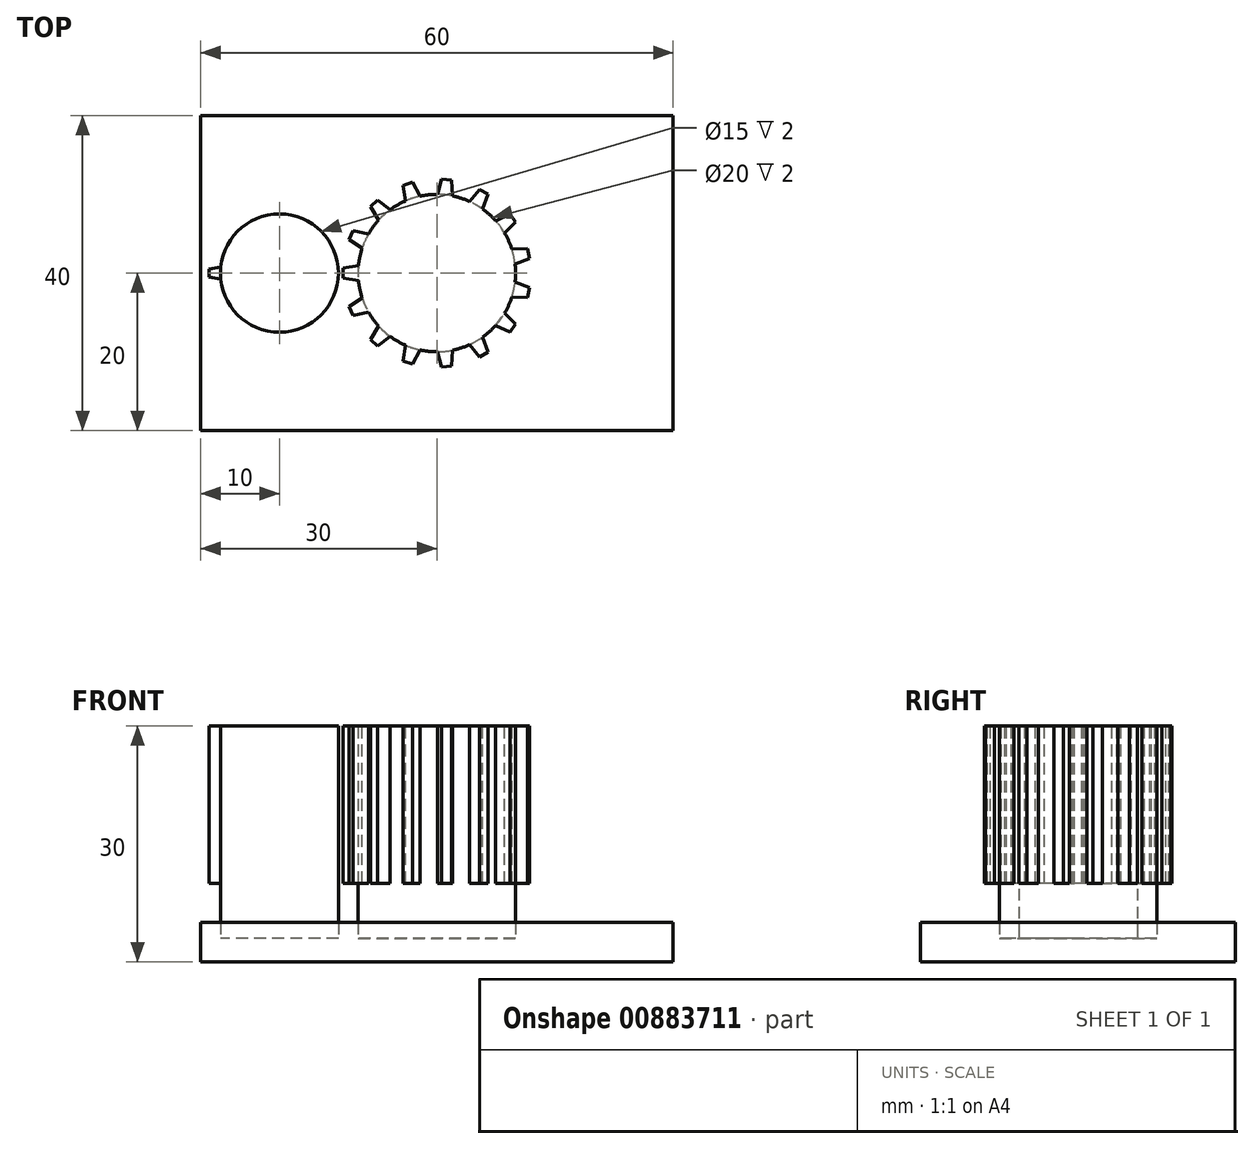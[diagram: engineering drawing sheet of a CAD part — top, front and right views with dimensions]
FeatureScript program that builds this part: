
annotation { "Feature Type Name" : "Feature", "Feature Type Description" : "" }
export const myFeature = defineFeature(function(context is Context, id is Id, definition is map)
    precondition{}
    {
        {
            var Q0;
            Q0=qCreatedBy(makeId("Top.planeOp"),FACE);
            var sketch = newSketch(context, id + "F0", { "sketchPlane" : qUnion([Q0])});
            skLineSegment(sketch, "E0.bottom", {"start": v(-30, 20) * mm, "end": v(30, 20) * mm});
            skLineSegment(sketch, "E0.top", {"start": v(-30, -20) * mm, "end": v(30, -20) * mm});
            skLineSegment(sketch, "E0.left", {"start": v(-30, 20) * mm, "end": v(-30, -20) * mm});
            skLineSegment(sketch, "E0.right", {"start": v(30, 20) * mm, "end": v(30, -20) * mm});
            skPoint(sketch, "E0.middle", {"position": v(0, 0) * mm});
            skSolve(sketch);
        }
        {
            var Q0;
            Q0 = qSketchRegion(id + "F0", true);
            extrude(context, id + "F1", {"entities" : qUnion([Q0]), "depth" : 5 * mm, "offsetDistance" : 25 * mm});
        }
        {
            var Q0;
            Q0=makeQuery(id+"F1.opExtrude","CAP_FACE",FACE,{"disambiguationData":[OSD([sQuery(id+"F0.wireOp",EDGE,"E0.bottom"),sQuery(id+"F0.wireOp",EDGE,"E0.top"),sQuery(id+"F0.wireOp",EDGE,"E0.left"),sQuery(id+"F0.wireOp",EDGE,"E0.right")])],"isStart":false});
            var sketch = newSketch(context, id + "F2", { "sketchPlane" : qUnion([Q0])});
            skCircle(sketch, "E1", {"center": v(-20, 0) * mm, "radius": 7.5 * mm});
            skSolve(sketch);
        }
        {
            var Q0;
            Q0 = qSketchRegion(id + "F2", true);
            extrude(context, id + "F3", {"entities" : qUnion([Q0]), "depth" : 25 * mm, "offsetDistance" : 25 * mm, "hasSecondDirection" : true, "secondDirectionOppositeDirection" : true, "secondDirectionDepth" : 2 * mm});
        }
        {
            var Q0;
            Q0=makeQuery(id+"F3.opExtrude","SWEPT_BODY",BODY,{"disambiguationData":[OSD([sQuery(id+"F2.wireOp",EDGE,"E1")])]});
            var Q1;
            Q1=makeQuery(id+"F1.opExtrude","SWEPT_BODY",BODY,{"disambiguationData":[OSD([sQuery(id+"F0.wireOp",EDGE,"E0.bottom"),sQuery(id+"F0.wireOp",EDGE,"E0.top"),sQuery(id+"F0.wireOp",EDGE,"E0.left"),sQuery(id+"F0.wireOp",EDGE,"E0.right")])]});
            booleanBodies(context, id + "F4", {"operationType" : BooleanOperationType.SUBTRACTION, "tools" : qUnion([Q0]), "targets" : qUnion([Q1]), "keepTools" : true});
        }
        {
            var Q0;
            Q0=makeQuery(id+"F1.opExtrude","CAP_FACE",FACE,{"disambiguationData":[OSD([sQuery(id+"F0.wireOp",EDGE,"E0.bottom"),sQuery(id+"F0.wireOp",EDGE,"E0.top"),sQuery(id+"F0.wireOp",EDGE,"E0.left"),sQuery(id+"F0.wireOp",EDGE,"E0.right")])],"isStart":false});
            var sketch = newSketch(context, id + "F5", { "sketchPlane" : qUnion([Q0])});
            skCircle(sketch, "E2", {"center": v(0, 0) * mm, "radius": 10 * mm});
            skSolve(sketch);
        }
        {
            var Q0;
            Q0 = qSketchRegion(id + "F5", true);
            extrude(context, id + "F6", {"entities" : qUnion([Q0]), "depth" : 25 * mm, "offsetDistance" : 25 * mm, "hasSecondDirection" : true, "secondDirectionOppositeDirection" : true, "secondDirectionDepth" : 2 * mm});
        }
        {
            var Q0;
            Q0=makeQuery(id+"F6.opExtrude","SWEPT_BODY",BODY,{"disambiguationData":[OSD([sQuery(id+"F5.wireOp",EDGE,"E2")])]});
            var Q1;
            Q1=makeQuery(id+"F1.opExtrude","SWEPT_BODY",BODY,{"disambiguationData":[OSD([sQuery(id+"F0.wireOp",EDGE,"E0.bottom"),sQuery(id+"F0.wireOp",EDGE,"E0.top"),sQuery(id+"F0.wireOp",EDGE,"E0.left"),sQuery(id+"F0.wireOp",EDGE,"E0.right")])]});
            booleanBodies(context, id + "F7", {"operationType" : BooleanOperationType.SUBTRACTION, "tools" : qUnion([Q0]), "targets" : qUnion([Q1]), "keepTools" : true});
        }
        {
            var Q0;
            Q0=makeQuery(id+"F3.opExtrude","CAP_FACE",FACE,{"disambiguationData":[OSD([sQuery(id+"F2.wireOp",EDGE,"E1")])],"isStart":false});
            var sketch = newSketch(context, id + "F8", { "sketchPlane" : qUnion([Q0])});
            skLineSegment(sketch, "E3", {"start": v(-27.46, 0.76) * mm, "end": v(-28.94, 0.5) * mm});
            skLineSegment(sketch, "E4", {"start": v(-28.94, 0.5) * mm, "end": v(-28.94, 0) * mm});
            skLineSegment(sketch, "E5.MirrorCS", {"start": v(-27.46, -0.76) * mm, "end": v(-28.94, -0.5) * mm});
            skLineSegment(sketch, "E6.MirrorCS", {"start": v(-28.94, -0.5) * mm, "end": v(-28.94, 0) * mm});
            skCircle(sketch, "E7.0", {"center": v(-20, 0) * mm, "radius": 7.5 * mm});
            skSolve(sketch);
        }
        {
            var Q0;
            Q0 = qSketchRegion(id + "F8", true);
            extrude(context, id + "F9", {"entities" : qUnion([Q0]), "oppositeDirection" : true, "depth" : 20 * mm, "offsetDistance" : 25 * mm});
        }
        {
            var Q0;
            Q0=makeQuery(id+"F3.opExtrude","SWEPT_BODY",BODY,{"disambiguationData":[OSD([sQuery(id+"F2.wireOp",EDGE,"E1")])]});
            var Q1;
            Q1=makeQuery(id+"F9.opExtrude","SWEPT_BODY",BODY,{"disambiguationData":[OSD([sQuery(id+"F8.wireOp",EDGE,"E3"),sQuery(id+"F8.wireOp",EDGE,"E4"),sQuery(id+"F8.wireOp",EDGE,"E5.MirrorCS"),sQuery(id+"F8.wireOp",EDGE,"E6.MirrorCS"),sQuery(id+"F8.wireOp",EDGE,"E7.0")])]});
            booleanBodies(context, id + "F10", {"operationType" : BooleanOperationType.SUBTRACTION, "tools" : qUnion([Q0]), "targets" : qUnion([Q1]), "keepTools" : true});
        }
        {
            var Q0;
            Q0=makeQuery(id+"F6.opExtrude","CAP_FACE",FACE,{"disambiguationData":[OSD([sQuery(id+"F5.wireOp",EDGE,"E2")])],"isStart":false});
            var sketch = newSketch(context, id + "F11", { "sketchPlane" : qUnion([Q0])});
            skCircle(sketch, "E8.0", {"center": v(0, 0) * mm, "radius": 10 * mm});
            skLineSegment(sketch, "E9", {"start": v(-9.95, 0.97) * mm, "end": v(-11.92, 0.63) * mm});
            skLineSegment(sketch, "E10", {"start": v(-11.92, 0.62) * mm, "end": v(-11.92, 0) * mm});
            skLineSegment(sketch, "E11.MirrorCS", {"start": v(-9.95, -0.97) * mm, "end": v(-11.92, -0.63) * mm});
            skLineSegment(sketch, "E12.MirrorCS", {"start": v(-11.92, -0.62) * mm, "end": v(-11.92, 0) * mm});
            skLineSegment(sketch, "E13.1.0", {"start": v(-9.49, -3.16) * mm, "end": v(-11.15, -4.28) * mm});
            skLineSegment(sketch, "E13.1.1", {"start": v(-11.15, -4.28) * mm, "end": v(-10.9, -4.85) * mm});
            skLineSegment(sketch, "E13.1.2", {"start": v(-10.64, -5.42) * mm, "end": v(-10.9, -4.85) * mm});
            skLineSegment(sketch, "E13.1.3", {"start": v(-8.7, -4.94) * mm, "end": v(-10.64, -5.42) * mm});
            skLineSegment(sketch, "E13.2.0", {"start": v(-7.38, -6.75) * mm, "end": v(-8.44, -8.44) * mm});
            skLineSegment(sketch, "E13.2.1", {"start": v(-8.44, -8.44) * mm, "end": v(-7.98, -8.86) * mm});
            skLineSegment(sketch, "E13.2.2", {"start": v(-7.51, -9.28) * mm, "end": v(-7.98, -8.86) * mm});
            skLineSegment(sketch, "E13.2.3", {"start": v(-5.94, -8.05) * mm, "end": v(-7.51, -9.28) * mm});
            skLineSegment(sketch, "E14.2.3.0", {"start": v(-4, -9.17) * mm, "end": v(-4.28, -11.15) * mm});
            skLineSegment(sketch, "E14.3.3.0", {"start": v(-4.28, -11.15) * mm, "end": v(-3.68, -11.34) * mm});
            skLineSegment(sketch, "E14.6.3.0", {"start": v(-3.09, -11.53) * mm, "end": v(-3.68, -11.34) * mm});
            skLineSegment(sketch, "E14.9.3.0", {"start": v(-2.15, -9.77) * mm, "end": v(-3.09, -11.53) * mm});
            skLineSegment(sketch, "E14.2.4.0", {"start": v(0.07, -10) * mm, "end": v(0.62, -11.92) * mm});
            skLineSegment(sketch, "E14.3.4.0", {"start": v(0.62, -11.92) * mm, "end": v(1.25, -11.86) * mm});
            skLineSegment(sketch, "E14.6.4.0", {"start": v(1.87, -11.8) * mm, "end": v(1.25, -11.86) * mm});
            skLineSegment(sketch, "E14.9.4.0", {"start": v(2, -9.8) * mm, "end": v(1.87, -11.8) * mm});
            skLineSegment(sketch, "E14.2.5.0", {"start": v(4.13, -9.1) * mm, "end": v(5.42, -10.64) * mm});
            skLineSegment(sketch, "E14.3.5.0", {"start": v(5.42, -10.64) * mm, "end": v(5.96, -10.32) * mm});
            skLineSegment(sketch, "E14.6.5.0", {"start": v(6.5, -10.01) * mm, "end": v(5.96, -10.32) * mm});
            skLineSegment(sketch, "E14.9.5.0", {"start": v(5.82, -8.13) * mm, "end": v(6.5, -10.01) * mm});
            skLineSegment(sketch, "E14.2.6.0", {"start": v(7.48, -6.64) * mm, "end": v(9.28, -7.51) * mm});
            skLineSegment(sketch, "E14.3.6.0", {"start": v(9.28, -7.51) * mm, "end": v(9.65, -7) * mm});
            skLineSegment(sketch, "E14.6.6.0", {"start": v(10.01, -6.5) * mm, "end": v(9.65, -7) * mm});
            skLineSegment(sketch, "E14.9.6.0", {"start": v(8.62, -5.06) * mm, "end": v(10.01, -6.5) * mm});
            skLineSegment(sketch, "E14.2.7.0", {"start": v(9.53, -3.02) * mm, "end": v(11.53, -3.1) * mm});
            skLineSegment(sketch, "E14.3.7.0", {"start": v(11.53, -3.1) * mm, "end": v(11.66, -2.48) * mm});
            skLineSegment(sketch, "E14.6.7.0", {"start": v(11.8, -1.87) * mm, "end": v(11.66, -2.48) * mm});
            skLineSegment(sketch, "E14.9.7.0", {"start": v(9.94, -1.12) * mm, "end": v(11.8, -1.87) * mm});
            skLineSegment(sketch, "E14.2.8.0", {"start": v(9.94, 1.12) * mm, "end": v(11.8, 1.87) * mm});
            skLineSegment(sketch, "E14.3.8.0", {"start": v(11.8, 1.87) * mm, "end": v(11.66, 2.48) * mm});
            skLineSegment(sketch, "E14.6.8.0", {"start": v(11.53, 3.1) * mm, "end": v(11.66, 2.48) * mm});
            skLineSegment(sketch, "E14.9.8.0", {"start": v(9.53, 3.02) * mm, "end": v(11.53, 3.1) * mm});
            skLineSegment(sketch, "E14.2.9.0", {"start": v(8.62, 5.06) * mm, "end": v(10.01, 6.5) * mm});
            skLineSegment(sketch, "E14.3.9.0", {"start": v(10.01, 6.5) * mm, "end": v(9.65, 7) * mm});
            skLineSegment(sketch, "E14.6.9.0", {"start": v(9.28, 7.51) * mm, "end": v(9.65, 7) * mm});
            skLineSegment(sketch, "E14.9.9.0", {"start": v(7.48, 6.64) * mm, "end": v(9.28, 7.51) * mm});
            skLineSegment(sketch, "E15.2.10.0", {"start": v(5.82, 8.13) * mm, "end": v(6.5, 10.01) * mm});
            skLineSegment(sketch, "E15.3.10.0", {"start": v(6.5, 10.01) * mm, "end": v(5.96, 10.32) * mm});
            skLineSegment(sketch, "E15.6.10.0", {"start": v(5.42, 10.64) * mm, "end": v(5.96, 10.32) * mm});
            skLineSegment(sketch, "E15.9.10.0", {"start": v(4.13, 9.1) * mm, "end": v(5.42, 10.64) * mm});
            skLineSegment(sketch, "E15.2.11.0", {"start": v(2, 9.8) * mm, "end": v(1.87, 11.8) * mm});
            skLineSegment(sketch, "E15.3.11.0", {"start": v(1.87, 11.8) * mm, "end": v(1.25, 11.86) * mm});
            skLineSegment(sketch, "E15.6.11.0", {"start": v(0.62, 11.92) * mm, "end": v(1.25, 11.86) * mm});
            skLineSegment(sketch, "E15.9.11.0", {"start": v(0.07, 10) * mm, "end": v(0.62, 11.92) * mm});
            skLineSegment(sketch, "E15.2.12.0", {"start": v(-2.15, 9.77) * mm, "end": v(-3.09, 11.53) * mm});
            skLineSegment(sketch, "E15.3.12.0", {"start": v(-3.09, 11.53) * mm, "end": v(-3.68, 11.34) * mm});
            skLineSegment(sketch, "E15.6.12.0", {"start": v(-4.28, 11.15) * mm, "end": v(-3.68, 11.34) * mm});
            skLineSegment(sketch, "E15.9.12.0", {"start": v(-4, 9.17) * mm, "end": v(-4.28, 11.15) * mm});
            skLineSegment(sketch, "E15.2.13.0", {"start": v(-5.94, 8.05) * mm, "end": v(-7.51, 9.28) * mm});
            skLineSegment(sketch, "E15.3.13.0", {"start": v(-7.51, 9.28) * mm, "end": v(-7.98, 8.86) * mm});
            skLineSegment(sketch, "E15.6.13.0", {"start": v(-8.44, 8.44) * mm, "end": v(-7.98, 8.86) * mm});
            skLineSegment(sketch, "E15.9.13.0", {"start": v(-7.38, 6.75) * mm, "end": v(-8.44, 8.44) * mm});
            skLineSegment(sketch, "E15.2.14.0", {"start": v(-8.7, 4.94) * mm, "end": v(-10.64, 5.42) * mm});
            skLineSegment(sketch, "E15.3.14.0", {"start": v(-10.64, 5.42) * mm, "end": v(-10.9, 4.85) * mm});
            skLineSegment(sketch, "E15.6.14.0", {"start": v(-11.15, 4.28) * mm, "end": v(-10.9, 4.85) * mm});
            skLineSegment(sketch, "E15.9.14.0", {"start": v(-9.49, 3.16) * mm, "end": v(-11.15, 4.28) * mm});
            skSolve(sketch);
        }
        {
            var Q0;
            Q0 = qSketchRegion(id + "F11", true);
            var Q1;
            Q1=makeQuery(id+"F6.opExtrude","CAP_FACE",FACE,{"disambiguationData":[OSD([sQuery(id+"F5.wireOp",EDGE,"E2")])],"isStart":true});
            extrude(context, id + "F12", {"entities" : qUnion([Q0]), "operationType" : NewBodyOperationType.ADD, "oppositeDirection" : true, "depth" : 20 * mm, "endBoundEntityFace" : qUnion([Q1]), "offsetDistance" : 25 * mm});
        }
    });
